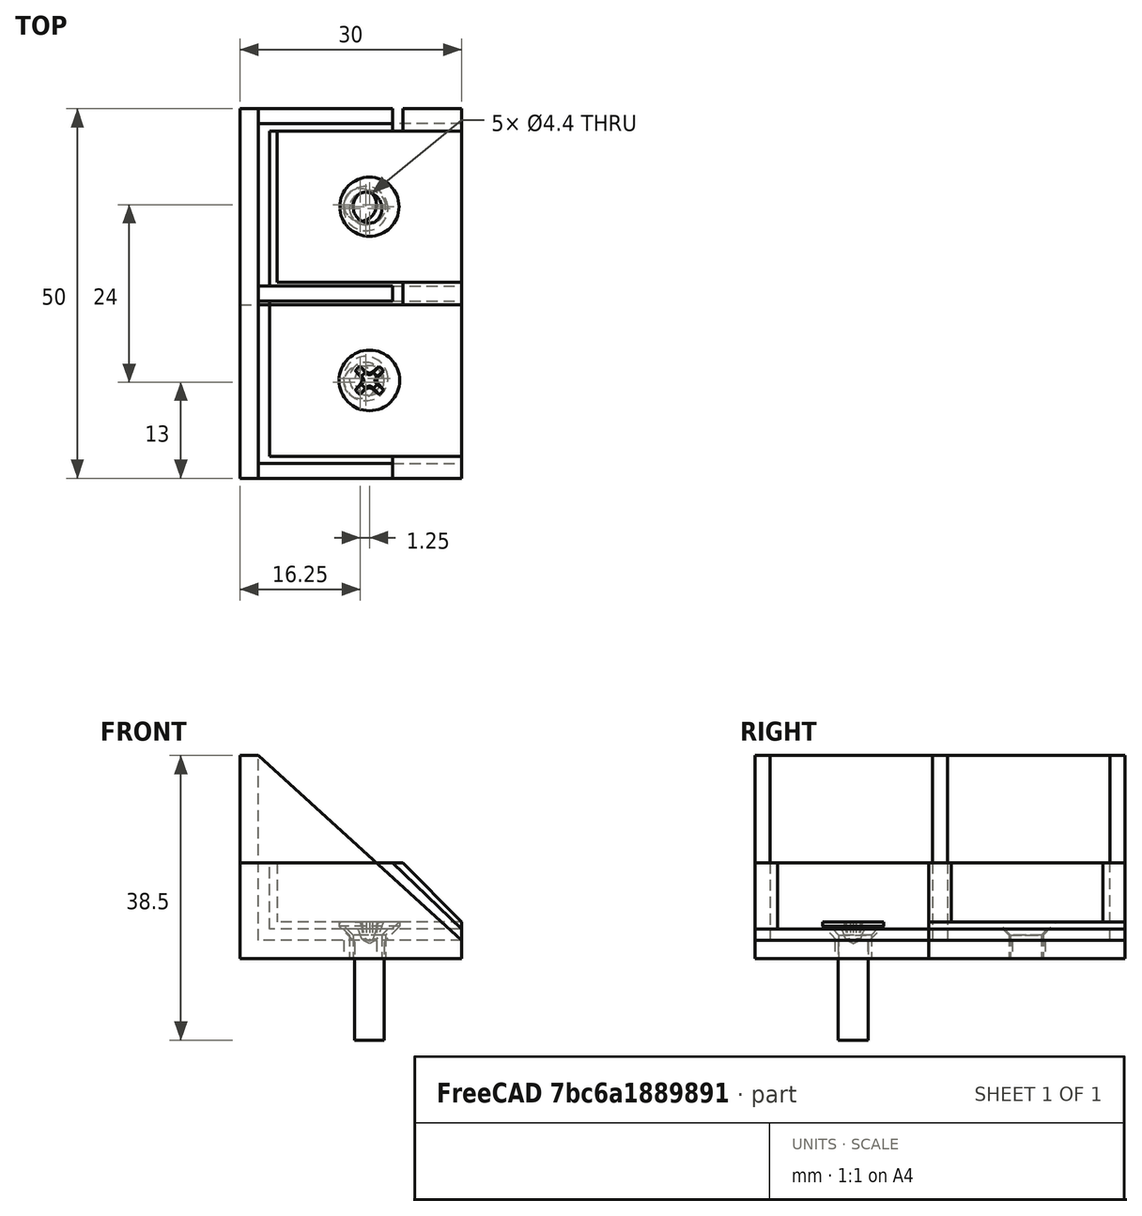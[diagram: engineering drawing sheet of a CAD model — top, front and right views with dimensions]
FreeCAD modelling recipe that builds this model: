
FCSTD DOCUMENT  (FreeCAD 0.18R4 (GitTag))
Label: triangulo_soporte_m4_para_armario
License: All rights reserved
LicenseURL: http://en.wikipedia.org/wiki/All_rights_reserved
objects: Sketcher::SketchObject×21, PartDesign::Pad×15, Mesh::Feature×4, PartDesign::Hole×3, PartDesign::Body×3, Spreadsheet::Sheet×3, PartDesign::Pocket×3, Part::FeaturePython×1, App::DocumentObjectGroup×1
note: 67 computed .brp shape members not serialized (recipe doc carries the construction recipe); baked Part::Feature solids carry a one-line shape summary decoded from their .brp

FEATURE [Sketcher::SketchObject] Sketch
  sketch-geometry (4):
    g0: LineSegment StartX=0 StartY=0 StartZ=0 EndX=30 EndY=0 EndZ=0
    g1: LineSegment StartX=30 StartY=0 StartZ=0 EndX=30 EndY=50 EndZ=0
    g2: LineSegment StartX=30 StartY=50 StartZ=0 EndX=0 EndY=50 EndZ=0
    g3: LineSegment StartX=0 StartY=50 StartZ=0 EndX=0 EndY=0 EndZ=0
  constraints (11):
    c: Coincident(g0,g1)
    c: Coincident(g1,g2)
    c: Coincident(g2,g3)
    c: Coincident(g3,g0)
    c: Horizontal(g0)
    c: Horizontal(g2)
    c: Vertical(g1)
    c: Vertical(g3)
    c: Coincident(g0,g-1)
    c: DistanceX(g0,g0) = 30
    c: DistanceY(g1,g1) = 50
FEATURE [PartDesign::Pad] Pad  label="Pad_base"
  Length = 2.5
  Length2 = 100
  Profile = -> Sketch
  Refine = true
  Type = 0
  expr: Length = Spreadsheet.a_pared
FEATURE [Sketcher::SketchObject] Sketch001
  ExternalGeometry = -> [Pad]
  Placement = pos=(0,0,0) rot=(0.57735,-0.57735,-0.57735;2.0944rad)
  sketch-geometry (4):
    g0: LineSegment StartX=0 StartY=2.5 StartZ=0 EndX=-50 EndY=2.5 EndZ=0
    g1: LineSegment StartX=-50 StartY=2.5 StartZ=0 EndX=-50 EndY=27.5 EndZ=0
    g2: LineSegment StartX=-50 StartY=27.5 StartZ=0 EndX=0 EndY=27.5 EndZ=0
    g3: LineSegment StartX=0 StartY=27.5 StartZ=0 EndX=0 EndY=2.5 EndZ=0
  constraints (10):
    c: Coincident(g0,g1)
    c: Coincident(g1,g2)
    c: Coincident(g2,g3)
    c: Coincident(g3,g0)
    c: Horizontal(g2)
    c: Vertical(g1)
    c: Vertical(g3)
    c: Coincident(g0,g-3)
    c: Coincident(g0,g-3)
    c: DistanceY(g1,g1) = 25
FEATURE [PartDesign::Pad] Pad001  label="Pad_lateral"
  BaseFeature = -> Pad
  Length = 2.5
  Length2 = 100
  Profile = -> Sketch001
  Refine = true
  Reversed = true
  Type = 0
  expr: Length = Spreadsheet.a_pared
FEATURE [Sketcher::SketchObject] Sketch002
  ExternalGeometry = -> [Pad001]
  Placement = pos=(0,0,0) rot=(1,0,0;1.5708rad)
  sketch-geometry (3):
    g0: LineSegment StartX=2.5 StartY=2.5 StartZ=0 EndX=2.5 EndY=27.5 EndZ=0
    g1: LineSegment StartX=2.5 StartY=27.5 StartZ=0 EndX=30 EndY=2.5 EndZ=0
    g2: LineSegment StartX=30 StartY=2.5 StartZ=0 EndX=2.5 EndY=2.5 EndZ=0
  constraints (6):
    c: Coincident(g-4,g0)
    c: Coincident(g0,g-3)
    c: Coincident(g0,g1)
    c: Coincident(g1,g-4)
    c: Coincident(g1,g2)
    c: Coincident(g2,g0)
FEATURE [PartDesign::Pad] Pad002  label="Pad_soporte_externo_1"
  BaseFeature = -> Pad001
  Length = 2
  Length2 = 100
  Profile = -> Sketch002
  Refine = true
  Reversed = true
  Type = 0
  expr: Length = Spreadsheet.a_soportes
FEATURE [Sketcher::SketchObject] Sketch003
  ExternalGeometry = -> [Pad002]
  Placement = pos=(0,25,0) rot=(1,0,0;1.5708rad)
  sketch-geometry (3):
    g0: LineSegment StartX=2.5 StartY=2.5 StartZ=0 EndX=2.5 EndY=27.5 EndZ=0
    g1: LineSegment StartX=2.5 StartY=27.5 StartZ=0 EndX=30 EndY=2.5 EndZ=0
    g2: LineSegment StartX=30 StartY=2.5 StartZ=0 EndX=2.5 EndY=2.5 EndZ=0
  constraints (6):
    c: Coincident(g-4,g0)
    c: Coincident(g0,g-3)
    c: Coincident(g0,g1)
    c: Coincident(g1,g-4)
    c: Coincident(g1,g2)
    c: Coincident(g2,g0)
FEATURE [PartDesign::Pad] Pad003  label="Pad_soporte_medio"
  BaseFeature = -> Pad002
  Length = 2
  Length2 = 100
  Midplane = true
  Profile = -> Sketch003
  Refine = true
  Type = 0
  expr: Length = Spreadsheet.a_sop_medio
FEATURE [Sketcher::SketchObject] Sketch004
  ExternalGeometry = -> [Pad003]
  Placement = pos=(0,50,0) rot=(1,0,0;1.5708rad)
  sketch-geometry (3):
    g0: LineSegment StartX=2.5 StartY=27.5 StartZ=0 EndX=2.5 EndY=2.5 EndZ=0
    g1: LineSegment StartX=2.5 StartY=2.5 StartZ=0 EndX=30 EndY=2.5 EndZ=0
    g2: LineSegment StartX=30 StartY=2.5 StartZ=0 EndX=2.5 EndY=27.5 EndZ=0
  constraints (6):
    c: Coincident(g-3,g0)
    c: Coincident(g0,g-4)
    c: Coincident(g0,g1)
    c: Coincident(g1,g2)
    c: Coincident(g2,g0)
    c: Coincident(g1,g-4)
FEATURE [PartDesign::Pad] Pad004  label="Pad_soporte_externo_2"
  BaseFeature = -> Pad003
  Length = 2
  Length2 = 100
  Profile = -> Sketch004
  Refine = true
  Type = 0
  expr: Length = Spreadsheet.a_soportes
FEATURE [Sketcher::SketchObject] Sketch005
  ExternalGeometry = -> [Pad004]
  Placement = pos=(0,0,5) rot=(0,0,1;0rad)
  sketch-geometry (4):
    g0: LineSegment [constr] StartX=2.5 StartY=2 StartZ=0 EndX=30 EndY=24 EndZ=0
    g1: LineSegment [constr] StartX=30 StartY=26 StartZ=0 EndX=2.5 EndY=48 EndZ=0
    g2: Circle CenterX=16.25 CenterY=37 CenterZ=0 NormalX=0 NormalY=0 NormalZ=1 AngleXU=0 Radius=1
    g3: Circle CenterX=16.25 CenterY=13 CenterZ=0 NormalX=0 NormalY=0 NormalZ=1 AngleXU=0 Radius=1
  constraints (9):
    c: Coincident(g0,g-3)
    c: Coincident(g0,g-4)
    c: Coincident(g1,g-5)
    c: Coincident(g1,g-6)
    c: PointOnObject(g3,g0)
    c: Radius(g2) = 1
    c: Equal(g2,g3)
    c: Symmetric(g1,g1,g2)
    c: Vertical(g2,g3)
FEATURE [PartDesign::Hole] Hole
  BaseFeature = -> Pad004
  Depth = 25
  DepthType = 0
  Diameter = 4.4
  DrillPoint = 1
  DrillPointAngle = 118
  HoleCutCountersinkAngle = 90
  HoleCutDepth = 0
  HoleCutDiameter = 8
  HoleCutType = 2
  ModelActualThread = false
  Profile = -> Sketch005
  Refine = true
  Tapered = false
  TaperedAngle = 90
  ThreadAngle = 0
  ThreadClass = 0
  ThreadCutOffInner = 0
  ThreadCutOffOuter = 0
  ThreadDirection = 0
  ThreadFit = 0
  ThreadPitch = 0
  ThreadSize = 5
  ThreadType = 1
  Threaded = false
FEATURE [PartDesign::Body] Body
  Group = -> [Pad,Pad001,Pad002,Pad003,Pad004,Hole]
  Origin = -> Origin
  Tip = -> Hole
FEATURE [Part::FeaturePython] Screw  label="M4x16-Screw"  # Fasteners workbench fastener (typed FeaturePython)
  Placement = pos=(17.5,13.25,5) rot=(0,0,1;0rad)
  diameter = 6
  invert = false
  length = 6
  lengthCustom = 16
  matchOuter = false
  offset = 0
  thread = false
  type = 34
FEATURE [Mesh::Feature] Mesh  label="Body_5_3_ (Meshed)"
FEATURE [Spreadsheet::Sheet] Spreadsheet
  cells = A1=ancho paredes; B1(a_pared)=2.5; A2=ancho soporte exteriores; B2(a_soportes)=2; A3=ancho soporte medio; B3(a_sop_medio)=2
FEATURE [Mesh::Feature] Mesh001  label="Body_2.5_2 (Meshed)"
FEATURE [Sketcher::SketchObject] Sketch011
  sketch-geometry (4):
    g0: LineSegment StartX=0 StartY=0 StartZ=0 EndX=30 EndY=0 EndZ=0
    g1: LineSegment StartX=30 StartY=0 StartZ=0 EndX=30 EndY=50 EndZ=0
    g2: LineSegment StartX=30 StartY=50 StartZ=0 EndX=0 EndY=50 EndZ=0
    g3: LineSegment StartX=0 StartY=50 StartZ=0 EndX=0 EndY=0 EndZ=0
  constraints (11):
    c: Coincident(g0,g1)
    c: Coincident(g1,g2)
    c: Coincident(g2,g3)
    c: Coincident(g3,g0)
    c: Horizontal(g0)
    c: Horizontal(g2)
    c: Vertical(g1)
    c: Vertical(g3)
    c: Coincident(g0,g-1)
    c: DistanceX(g0,g0) = 30
    c: DistanceY(g1,g1) = 50
FEATURE [PartDesign::Pad] Pad009  label="Pad_base001"
  Length = 4
  Length2 = 100
  Profile = -> Sketch011
  Refine = true
  Type = 0
  expr: Length = Spreadsheet001.a_pared
FEATURE [Sketcher::SketchObject] Sketch007
  ExternalGeometry = -> [Pad009]
  Placement = pos=(0,0,0) rot=(0.57735,-0.57735,-0.57735;2.0944rad)
  sketch-geometry (4):
    g0: LineSegment StartX=0 StartY=4 StartZ=0 EndX=-50 EndY=4 EndZ=0
    g1: LineSegment StartX=-50 StartY=4 StartZ=0 EndX=-50 EndY=29 EndZ=0
    g2: LineSegment StartX=-50 StartY=29 StartZ=0 EndX=0 EndY=29 EndZ=0
    g3: LineSegment StartX=0 StartY=29 StartZ=0 EndX=0 EndY=4 EndZ=0
  constraints (10):
    c: Coincident(g0,g1)
    c: Coincident(g1,g2)
    c: Coincident(g2,g3)
    c: Coincident(g3,g0)
    c: Horizontal(g2)
    c: Vertical(g1)
    c: Vertical(g3)
    c: Coincident(g0,g-3)
    c: Coincident(g0,g-3)
    c: DistanceY(g1,g1) = 25
FEATURE [PartDesign::Pad] Pad006  label="Pad_lateral001"
  BaseFeature = -> Pad009
  Length = 4
  Length2 = 100
  Profile = -> Sketch007
  Refine = true
  Reversed = true
  Type = 0
  expr: Length = Spreadsheet001.a_pared
FEATURE [Sketcher::SketchObject] Sketch008
  ExternalGeometry = -> [Pad006]
  Placement = pos=(0,0,0) rot=(1,0,0;1.5708rad)
  sketch-geometry (3):
    g0: LineSegment StartX=4 StartY=4 StartZ=0 EndX=4 EndY=29 EndZ=0
    g1: LineSegment StartX=4 StartY=29 StartZ=0 EndX=30 EndY=4 EndZ=0
    g2: LineSegment StartX=30 StartY=4 StartZ=0 EndX=4 EndY=4 EndZ=0
  constraints (6):
    c: Coincident(g-4,g0)
    c: Coincident(g0,g-3)
    c: Coincident(g0,g1)
    c: Coincident(g1,g-4)
    c: Coincident(g1,g2)
    c: Coincident(g2,g0)
FEATURE [PartDesign::Pad] Pad007  label="Pad_soporte_externo_003"
  BaseFeature = -> Pad006
  Length = 3
  Length2 = 100
  Profile = -> Sketch008
  Refine = true
  Reversed = true
  Type = 0
  expr: Length = Spreadsheet001.a_soportes
FEATURE [Sketcher::SketchObject] Sketch009
  ExternalGeometry = -> [Pad007]
  Placement = pos=(0,25,0) rot=(1,0,0;1.5708rad)
  sketch-geometry (3):
    g0: LineSegment StartX=4 StartY=4 StartZ=0 EndX=4 EndY=29 EndZ=0
    g1: LineSegment StartX=4 StartY=29 StartZ=0 EndX=30 EndY=4 EndZ=0
    g2: LineSegment StartX=30 StartY=4 StartZ=0 EndX=4 EndY=4 EndZ=0
  constraints (6):
    c: Coincident(g-4,g0)
    c: Coincident(g0,g-3)
    c: Coincident(g0,g1)
    c: Coincident(g1,g-4)
    c: Coincident(g1,g2)
    c: Coincident(g2,g0)
FEATURE [PartDesign::Pad] Pad005  label="Pad_soporte_medio001"
  BaseFeature = -> Pad007
  Length = 2
  Length2 = 100
  Midplane = true
  Profile = -> Sketch009
  Refine = true
  Type = 0
  expr: Length = Spreadsheet001.a_sop_medio
FEATURE [Sketcher::SketchObject] Sketch006
  ExternalGeometry = -> [Pad005]
  Placement = pos=(0,50,0) rot=(1,0,0;1.5708rad)
  sketch-geometry (3):
    g0: LineSegment StartX=4 StartY=29 StartZ=0 EndX=4 EndY=4 EndZ=0
    g1: LineSegment StartX=4 StartY=4 StartZ=0 EndX=30 EndY=4 EndZ=0
    g2: LineSegment StartX=30 StartY=4 StartZ=0 EndX=4 EndY=29 EndZ=0
  constraints (6):
    c: Coincident(g-3,g0)
    c: Coincident(g0,g-4)
    c: Coincident(g0,g1)
    c: Coincident(g1,g2)
    c: Coincident(g2,g0)
    c: Coincident(g1,g-4)
FEATURE [PartDesign::Pad] Pad008  label="Pad_soporte_externo_004"
  BaseFeature = -> Pad005
  Length = 3
  Length2 = 100
  Profile = -> Sketch006
  Refine = true
  Type = 0
  expr: Length = Spreadsheet001.a_soportes
FEATURE [Sketcher::SketchObject] Sketch010
  ExternalGeometry = -> [Pad008]
  Placement = pos=(0,0,5) rot=(0,0,1;0rad)
  sketch-geometry (4):
    g0: LineSegment [constr] StartX=4 StartY=3 StartZ=0 EndX=30 EndY=24 EndZ=0
    g1: LineSegment [constr] StartX=30 StartY=26 StartZ=0 EndX=4 EndY=47 EndZ=0
    g2: Circle CenterX=17 CenterY=36.5 CenterZ=0 NormalX=0 NormalY=0 NormalZ=1 AngleXU=0 Radius=1
    g3: Circle CenterX=17 CenterY=13.5 CenterZ=0 NormalX=0 NormalY=0 NormalZ=1 AngleXU=0 Radius=1
  constraints (9):
    c: Coincident(g0,g-3)
    c: Coincident(g0,g-4)
    c: Coincident(g1,g-5)
    c: Coincident(g1,g-6)
    c: PointOnObject(g3,g0)
    c: Radius(g2) = 1
    c: Equal(g2,g3)
    c: Symmetric(g1,g1,g2)
    c: Vertical(g2,g3)
FEATURE [PartDesign::Hole] Hole001
  BaseFeature = -> Pad008
  Depth = 25
  DepthType = 0
  Diameter = 4.4
  DrillPoint = 1
  DrillPointAngle = 118
  HoleCutCountersinkAngle = 90
  HoleCutDepth = 0
  HoleCutDiameter = 8
  HoleCutType = 2
  ModelActualThread = false
  Profile = -> Sketch010
  Refine = true
  Tapered = false
  TaperedAngle = 90
  ThreadAngle = 0
  ThreadClass = 0
  ThreadCutOffInner = 0
  ThreadCutOffOuter = 0
  ThreadDirection = 0
  ThreadFit = 0
  ThreadPitch = 0
  ThreadSize = 5
  ThreadType = 1
  Threaded = false
FEATURE [Spreadsheet::Sheet] Spreadsheet001
  cells = A1=ancho paredes; B1(a_pared)=4; A2=ancho soporte exteriores; B2(a_soportes)=3; A3=ancho soporte medio; B3(a_sop_medio)=2
FEATURE [Sketcher::SketchObject] Sketch012
  Placement = pos=(0,0,13) rot=(0,0,1;0rad)
  sketch-geometry (4):
    g0: LineSegment StartX=-5.63377 StartY=53.5232 StartZ=0 EndX=35.2668 EndY=53.5232 EndZ=0
    g1: LineSegment StartX=35.2668 StartY=53.5232 StartZ=0 EndX=35.2668 EndY=-2.99002 EndZ=0
    g2: LineSegment StartX=35.2668 StartY=-2.99002 StartZ=0 EndX=-5.63377 EndY=-2.99002 EndZ=0
    g3: LineSegment StartX=-5.63377 StartY=-2.99002 StartZ=0 EndX=-5.63377 EndY=53.5232 EndZ=0
  constraints (8):
    c: Coincident(g0,g1)
    c: Coincident(g1,g2)
    c: Coincident(g2,g3)
    c: Coincident(g3,g0)
    c: Horizontal(g0)
    c: Horizontal(g2)
    c: Vertical(g1)
    c: Vertical(g3)
FEATURE [PartDesign::Pocket] Pocket
  BaseFeature = -> Hole001
  Length = 25
  Length2 = 100
  Profile = -> Sketch012
  Refine = true
  Reversed = true
  Type = 0
FEATURE [PartDesign::Body] Body001  label="Body_para_cajon"
  Group = -> [Pad009,Pad006,Pad007,Pad005,Pad008,Hole001,Pocket]
  Origin = -> Origin001
  Tip = -> Pocket
FEATURE [Mesh::Feature] Mesh002  label="Body_para_cajon _4_3_2_(Meshed)"
FEATURE [Spreadsheet::Sheet] Spreadsheet002
  cells = A1=ancho paredes; B1(a_pared)=5; A2=ancho soporte exteriores; B2(a_soportes)=3; A3=ancho soporte medio; B3(a_sop_medio)=3
FEATURE [Sketcher::SketchObject] Sketch015
  sketch-geometry (4):
    g0: LineSegment StartX=0 StartY=0 StartZ=0 EndX=30 EndY=0 EndZ=0
    g1: LineSegment StartX=30 StartY=0 StartZ=0 EndX=30 EndY=50 EndZ=0
    g2: LineSegment StartX=30 StartY=50 StartZ=0 EndX=0 EndY=50 EndZ=0
    g3: LineSegment StartX=0 StartY=50 StartZ=0 EndX=0 EndY=0 EndZ=0
  constraints (11):
    c: Coincident(g0,g1)
    c: Coincident(g1,g2)
    c: Coincident(g2,g3)
    c: Coincident(g3,g0)
    c: Horizontal(g0)
    c: Horizontal(g2)
    c: Vertical(g1)
    c: Vertical(g3)
    c: Coincident(g0,g-1)
    c: DistanceX(g0,g0) = 30
    c: DistanceY(g1,g1) = 50
FEATURE [PartDesign::Pad] Pad014  label="Pad_base002"
  Length = 5
  Length2 = 100
  Profile = -> Sketch015
  Refine = true
  Type = 0
  expr: Length = Spreadsheet002.a_pared
FEATURE [Sketcher::SketchObject] Sketch016
  ExternalGeometry = -> [Pad014]
  Placement = pos=(0,0,0) rot=(0.57735,-0.57735,-0.57735;2.0944rad)
  sketch-geometry (4):
    g0: LineSegment StartX=0 StartY=5 StartZ=0 EndX=-50 EndY=5 EndZ=0
    g1: LineSegment StartX=-50 StartY=5 StartZ=0 EndX=-50 EndY=30 EndZ=0
    g2: LineSegment StartX=-50 StartY=30 StartZ=0 EndX=0 EndY=30 EndZ=0
    g3: LineSegment StartX=0 StartY=30 StartZ=0 EndX=0 EndY=5 EndZ=0
  constraints (10):
    c: Coincident(g0,g1)
    c: Coincident(g1,g2)
    c: Coincident(g2,g3)
    c: Coincident(g3,g0)
    c: Horizontal(g2)
    c: Vertical(g1)
    c: Vertical(g3)
    c: Coincident(g0,g-3)
    c: Coincident(g0,g-3)
    c: DistanceY(g1,g1) = 25
FEATURE [PartDesign::Pad] Pad013  label="Pad_lateral002"
  BaseFeature = -> Pad014
  Length = 5
  Length2 = 100
  Profile = -> Sketch016
  Refine = true
  Reversed = true
  Type = 0
  expr: Length = Spreadsheet002.a_pared
FEATURE [Sketcher::SketchObject] Sketch014
  ExternalGeometry = -> [Pad013]
  Placement = pos=(0,0,0) rot=(1,0,0;1.5708rad)
  sketch-geometry (3):
    g0: LineSegment StartX=5 StartY=5 StartZ=0 EndX=5 EndY=30 EndZ=0
    g1: LineSegment StartX=5 StartY=30 StartZ=0 EndX=30 EndY=5 EndZ=0
    g2: LineSegment StartX=30 StartY=5 StartZ=0 EndX=5 EndY=5 EndZ=0
  constraints (6):
    c: Coincident(g-4,g0)
    c: Coincident(g0,g-3)
    c: Coincident(g0,g1)
    c: Coincident(g1,g-4)
    c: Coincident(g1,g2)
    c: Coincident(g2,g0)
FEATURE [PartDesign::Pad] Pad010  label="Pad_soporte_externo_005"
  BaseFeature = -> Pad013
  Length = 3
  Length2 = 100
  Profile = -> Sketch014
  Refine = true
  Reversed = true
  Type = 0
  expr: Length = Spreadsheet002.a_soportes
FEATURE [Sketcher::SketchObject] Sketch017
  ExternalGeometry = -> [Pad010]
  Placement = pos=(0,25,0) rot=(1,0,0;1.5708rad)
  sketch-geometry (3):
    g0: LineSegment StartX=5 StartY=5 StartZ=0 EndX=5 EndY=30 EndZ=0
    g1: LineSegment StartX=5 StartY=30 StartZ=0 EndX=30 EndY=5 EndZ=0
    g2: LineSegment StartX=30 StartY=5 StartZ=0 EndX=5 EndY=5 EndZ=0
  constraints (6):
    c: Coincident(g-4,g0)
    c: Coincident(g0,g-3)
    c: Coincident(g0,g1)
    c: Coincident(g1,g-4)
    c: Coincident(g1,g2)
    c: Coincident(g2,g0)
FEATURE [PartDesign::Pad] Pad011  label="Pad_soporte_medio002"
  BaseFeature = -> Pad010
  Length = 3
  Length2 = 100
  Midplane = true
  Profile = -> Sketch017
  Refine = true
  Type = 0
  expr: Length = Spreadsheet002.a_sop_medio
FEATURE [Sketcher::SketchObject] Sketch013
  ExternalGeometry = -> [Pad011]
  Placement = pos=(0,50,0) rot=(1,0,0;1.5708rad)
  sketch-geometry (3):
    g0: LineSegment StartX=5 StartY=30 StartZ=0 EndX=5 EndY=5 EndZ=0
    g1: LineSegment StartX=5 StartY=5 StartZ=0 EndX=30 EndY=5 EndZ=0
    g2: LineSegment StartX=30 StartY=5 StartZ=0 EndX=5 EndY=30 EndZ=0
  constraints (6):
    c: Coincident(g-3,g0)
    c: Coincident(g0,g-4)
    c: Coincident(g0,g1)
    c: Coincident(g1,g2)
    c: Coincident(g2,g0)
    c: Coincident(g1,g-4)
FEATURE [PartDesign::Pad] Pad012  label="Pad_soporte_externo_006"
  BaseFeature = -> Pad011
  Length = 3
  Length2 = 100
  Profile = -> Sketch013
  Refine = true
  Type = 0
  expr: Length = Spreadsheet002.a_soportes
FEATURE [Sketcher::SketchObject] Sketch018
  Placement = pos=(0,0,13) rot=(0,0,1;0rad)
  sketch-geometry (4):
    g0: LineSegment StartX=-5.63377 StartY=53.5232 StartZ=0 EndX=35.2668 EndY=53.5232 EndZ=0
    g1: LineSegment StartX=35.2668 StartY=53.5232 StartZ=0 EndX=35.2668 EndY=-2.99002 EndZ=0
    g2: LineSegment StartX=35.2668 StartY=-2.99002 StartZ=0 EndX=-5.63377 EndY=-2.99002 EndZ=0
    g3: LineSegment StartX=-5.63377 StartY=-2.99002 StartZ=0 EndX=-5.63377 EndY=53.5232 EndZ=0
  constraints (8):
    c: Coincident(g0,g1)
    c: Coincident(g1,g2)
    c: Coincident(g2,g3)
    c: Coincident(g3,g0)
    c: Horizontal(g0)
    c: Horizontal(g2)
    c: Vertical(g1)
    c: Vertical(g3)
FEATURE [Sketcher::SketchObject] Sketch019
  ExternalGeometry = -> [Pad012]
  Placement = pos=(0,0,5) rot=(0,0,1;0rad)
  sketch-geometry (4):
    g0: LineSegment [constr] StartX=5 StartY=3 StartZ=0 EndX=30 EndY=23.5 EndZ=0
    g1: LineSegment [constr] StartX=30 StartY=26.5 StartZ=0 EndX=5 EndY=47 EndZ=0
    g2: Circle CenterX=17.5 CenterY=36.75 CenterZ=0 NormalX=0 NormalY=0 NormalZ=1 AngleXU=0 Radius=1
    g3: Circle CenterX=17.5 CenterY=13.25 CenterZ=0 NormalX=0 NormalY=0 NormalZ=1 AngleXU=0 Radius=1
  constraints (9):
    c: Coincident(g0,g-3)
    c: Coincident(g0,g-4)
    c: Coincident(g1,g-5)
    c: Coincident(g1,g-6)
    c: PointOnObject(g3,g0)
    c: Radius(g2) = 1
    c: Equal(g2,g3)
    c: Symmetric(g1,g1,g2)
    c: Vertical(g2,g3)
FEATURE [PartDesign::Hole] Hole002
  BaseFeature = -> Pad012
  Depth = 25
  DepthType = 0
  Diameter = 4.4
  DrillPoint = 1
  DrillPointAngle = 118
  HoleCutCountersinkAngle = 90
  HoleCutDepth = 0
  HoleCutDiameter = 8
  HoleCutType = 2
  ModelActualThread = false
  Profile = -> Sketch019
  Refine = true
  Tapered = false
  TaperedAngle = 90
  ThreadAngle = 0
  ThreadClass = 0
  ThreadCutOffInner = 0
  ThreadCutOffOuter = 0
  ThreadDirection = 0
  ThreadFit = 0
  ThreadPitch = 0
  ThreadSize = 5
  ThreadType = 1
  Threaded = false
FEATURE [PartDesign::Pocket] Pocket001
  BaseFeature = -> Hole002
  Length = 25
  Length2 = 100
  Profile = -> Sketch018
  Refine = true
  Reversed = true
  Type = 0
FEATURE [Sketcher::SketchObject] Sketch020
  Placement = pos=(0,0,0) rot=(-1,0,0;4.71239rad)
  sketch-geometry (4):
    g0: LineSegment StartX=-8.85724 StartY=24.6854 StartZ=0 EndX=36.5771 EndY=24.6854 EndZ=0
    g1: LineSegment StartX=36.5771 StartY=24.6854 StartZ=0 EndX=36.5771 EndY=-9.75936 EndZ=0
    g2: LineSegment StartX=36.5771 StartY=-9.75936 StartZ=0 EndX=-8.85724 EndY=-9.75936 EndZ=0
    g3: LineSegment StartX=-8.85724 StartY=-9.75936 StartZ=0 EndX=-8.85724 EndY=24.6854 EndZ=0
  constraints (8):
    c: Coincident(g0,g1)
    c: Coincident(g1,g2)
    c: Coincident(g2,g3)
    c: Coincident(g3,g0)
    c: Horizontal(g0)
    c: Horizontal(g2)
    c: Vertical(g1)
    c: Vertical(g3)
FEATURE [App::DocumentObjectGroup] Group  label="sketches"
  Group = -> [Sketch,Sketch001,Sketch002,Sketch005,Sketch012,Sketch020]
FEATURE [PartDesign::Pocket] Pocket002
  BaseFeature = -> Pocket001
  Length = 23.5
  Length2 = 100
  Profile = -> Sketch020
  Refine = true
  Type = 0
FEATURE [PartDesign::Body] Body002  label="Body_para_cajon001"
  Group = -> [Pad014,Pad013,Pad010,Pad011,Pad012,Hole002,Pocket001,Pocket002]
  Origin = -> Origin002
  Tip = -> Pocket002
FEATURE [Mesh::Feature] Mesh003  label="small_5_3 (Meshed)"
